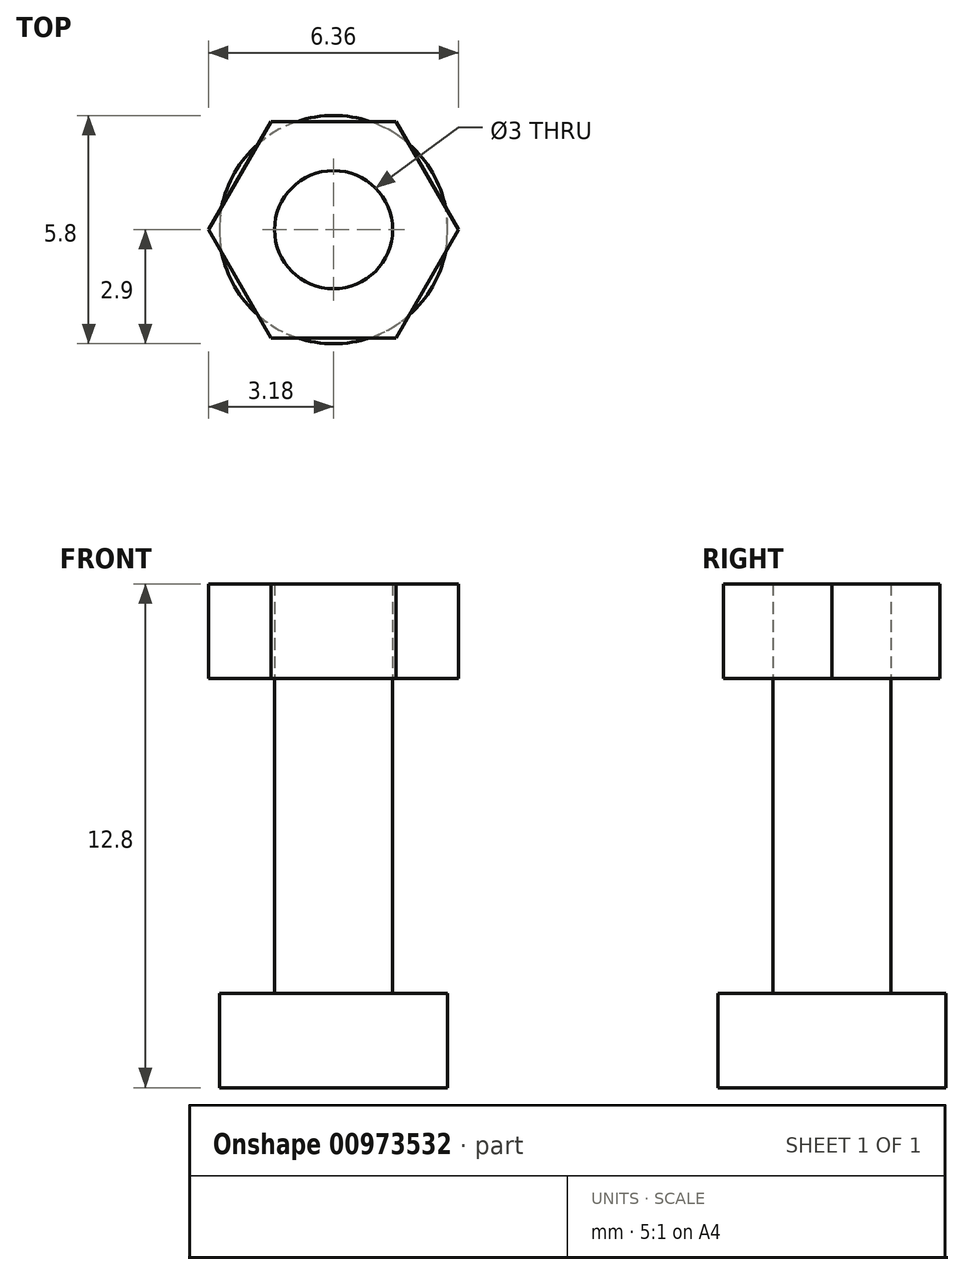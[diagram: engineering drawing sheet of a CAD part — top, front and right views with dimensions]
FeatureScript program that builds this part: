
annotation { "Feature Type Name" : "Feature", "Feature Type Description" : "" }
export const myFeature = defineFeature(function(context is Context, id is Id, definition is map)
    precondition{}
    {
        {
            var Q0;
            Q0=qCreatedBy(makeId("Top.planeOp"),FACE);
            var sketch = newSketch(context, id + "F0", { "sketchPlane" : qUnion([Q0])});
            skCircle(sketch, "E0", {"center": v(0, 0) * mm, "radius": 1.5 * mm});
            skCircle(sketch, "E1", {"center": v(0, 0) * mm, "radius": 2.9 * mm});
            skSolve(sketch);
        }
        {
            var Q0;
            Q0=makeQuery(id+"F0.imprint","IMPRINT",FACE,{"disambiguationData":[TD([[makeQuery(id+"F0.imprint","IMPRINT",EDGE,{"derivedFrom":sQuery(id+"F0.wireOp",EDGE,"E0")}),1.0]])]});
            extrude(context, id + "F1", {"entities" : qUnion([Q0]), "depth" : 10.4 * mm, "offsetDistance" : 25 * mm});
        }
        {
            var Q0;
            Q0=makeQuery(id+"F0.imprint","IMPRINT",FACE,{"disambiguationData":[TD([[makeQuery(id+"F0.imprint","IMPRINT",EDGE,{"derivedFrom":sQuery(id+"F0.wireOp",EDGE,"E0")}),-1.0]])]});
            extrude(context, id + "F2", {"entities" : qUnion([Q0]), "operationType" : NewBodyOperationType.ADD, "depth" : 2.4 * mm, "offsetDistance" : 25 * mm});
        }
        {
            var Q0;
            Q0=makeQuery(id+"F1.opExtrude","CAP_FACE",FACE,{"disambiguationData":[OSD([sQuery(id+"F0.wireOp",EDGE,"E0")])],"isStart":false});
            var sketch = newSketch(context, id + "F3", { "sketchPlane" : qUnion([Q0])});
            skCircle(sketch, "E2.cCircle", {"center": v(0, 0) * mm, "radius": 2.75 * mm, "construction": true});
            skLineSegment(sketch, "E2.0", {"start": v(1.59, 2.75) * mm, "end": v(3.18, 0) * mm});
            skLineSegment(sketch, "E2.1", {"start": v(3.18, 0) * mm, "end": v(1.59, -2.75) * mm});
            skLineSegment(sketch, "E2.2", {"start": v(1.59, -2.75) * mm, "end": v(-1.59, -2.75) * mm});
            skLineSegment(sketch, "E2.3", {"start": v(-1.59, -2.75) * mm, "end": v(-3.18, 0) * mm});
            skLineSegment(sketch, "E2.4", {"start": v(-3.18, 0) * mm, "end": v(-1.59, 2.75) * mm});
            skLineSegment(sketch, "E2.5", {"start": v(-1.59, 2.75) * mm, "end": v(1.59, 2.75) * mm});
            skPoint(sketch, "E2.0.midPoint", {"position": v(2.38, 1.37) * mm});
            skCircle(sketch, "E3", {"center": v(0, 0) * mm, "radius": 1.5 * mm});
            skSolve(sketch);
        }
        {
            var Q0;
            Q0 = qSketchRegion(id + "F3", true);
            extrude(context, id + "F4", {"entities" : qUnion([Q0]), "depth" : 2.4 * mm, "offsetDistance" : 25 * mm});
        }
    });
